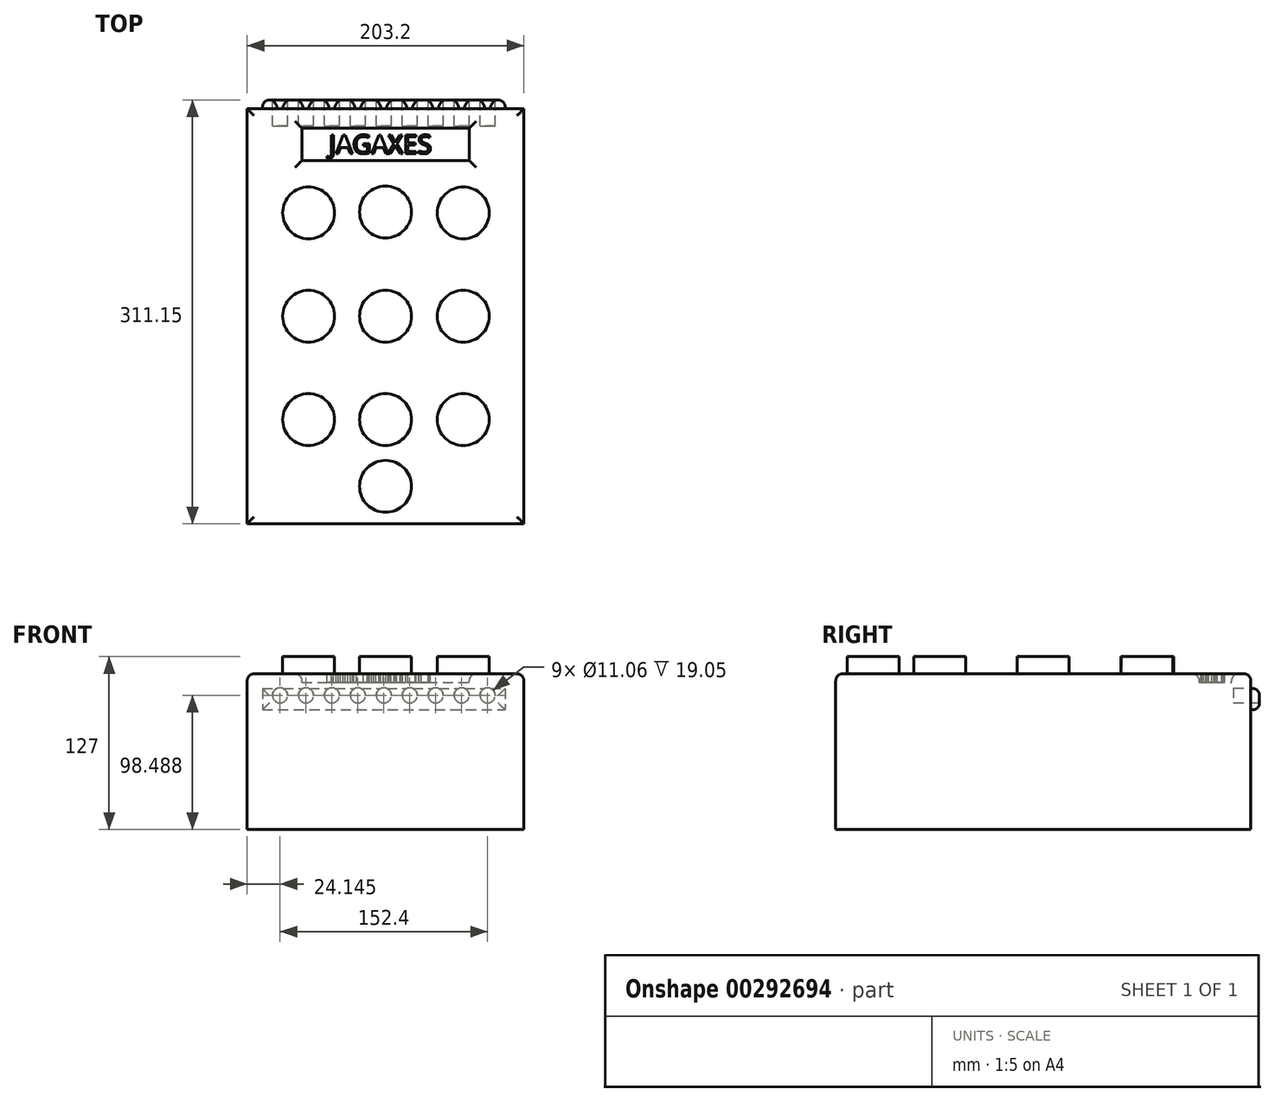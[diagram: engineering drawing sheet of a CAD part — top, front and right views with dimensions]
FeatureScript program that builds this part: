
annotation { "Feature Type Name" : "Feature", "Feature Type Description" : "" }
export const myFeature = defineFeature(function(context is Context, id is Id, definition is map)
    precondition{}
    {
        {
            var Q0;
            Q0=qCreatedBy(makeId("Top.planeOp"),FACE);
            var sketch = newSketch(context, id + "F0", { "sketchPlane" : qUnion([Q0])});
            skLineSegment(sketch, "E0.bottom", {"start": v(-101.6, 152.4) * mm, "end": v(101.6, 152.4) * mm});
            skLineSegment(sketch, "E0.top", {"start": v(-101.6, -152.4) * mm, "end": v(101.6, -152.4) * mm});
            skLineSegment(sketch, "E0.left", {"start": v(-101.6, 152.4) * mm, "end": v(-101.6, -152.4) * mm});
            skLineSegment(sketch, "E0.right", {"start": v(101.6, 152.4) * mm, "end": v(101.6, -152.4) * mm});
            skPoint(sketch, "E0.middle", {"position": v(0, 0) * mm});
            skSolve(sketch);
        }
        {
            var Q0;
            Q0=makeQuery(id+"F0.imprint","IMPRINT",FACE,{"disambiguationData":[TD([[makeQuery(id+"F0.imprint","IMPRINT",EDGE,{"derivedFrom":sQuery(id+"F0.wireOp",EDGE,"E0.bottom")}),-1.0]])]});
            extrude(context, id + "F1", {"entities" : qUnion([Q0]), "oppositeDirection" : true, "depth" : 114.3 * mm});
        }
        {
            var Q0;
            Q0=qCreatedBy(makeId("Top.planeOp"),FACE);
            var sketch = newSketch(context, id + "F2", { "sketchPlane" : qUnion([Q0])});
            skCircle(sketch, "E1", {"center": v(-56.48, 75.93) * mm, "radius": 19.05 * mm});
            skCircle(sketch, "E2", {"center": v(0, 76.56) * mm, "radius": 19.05 * mm});
            skCircle(sketch, "E3", {"center": v(57.1, 75.93) * mm, "radius": 19.05 * mm});
            skSolve(sketch);
        }
        {
            var Q0;
            Q0=makeQuery(id+"F2.imprint","IMPRINT",FACE,{"disambiguationData":[TD([[makeQuery(id+"F2.imprint","IMPRINT",EDGE,{"derivedFrom":sQuery(id+"F2.wireOp",EDGE,"E1")}),1.0]])]});
            extrude(context, id + "F3", {"entities" : qUnion([Q0]), "operationType" : NewBodyOperationType.ADD, "depth" : 12.7 * mm});
        }
        {
            var Q0;
            Q0 = qSketchRegion(id + "F2", true);
            extrude(context, id + "F4", {"entities" : qUnion([Q0]), "operationType" : NewBodyOperationType.ADD, "depth" : 12.7 * mm});
        }
        {
            var Q0;
            Q0=makeQuery(id+"F1.opExtrude","CAP_FACE",FACE,{"disambiguationData":[OSD([sQuery(id+"F0.wireOp",EDGE,"E0.bottom"),sQuery(id+"F0.wireOp",EDGE,"E0.top"),sQuery(id+"F0.wireOp",EDGE,"E0.left"),sQuery(id+"F0.wireOp",EDGE,"E0.right")])],"isStart":true});
            var sketch = newSketch(context, id + "F5", { "sketchPlane" : qUnion([Q0])});
            skCircle(sketch, "E4", {"center": v(0, 0) * mm, "radius": 19.05 * mm});
            skCircle(sketch, "E5", {"center": v(57.1, 0) * mm, "radius": 19.05 * mm});
            skCircle(sketch, "E6", {"center": v(-56.48, 0) * mm, "radius": 19.05 * mm});
            skCircle(sketch, "E7", {"center": v(-56.48, -75.93) * mm, "radius": 19.05 * mm});
            skCircle(sketch, "E8", {"center": v(0, -75.93) * mm, "radius": 19.05 * mm});
            skCircle(sketch, "E9", {"center": v(57.1, -75.93) * mm, "radius": 19.05 * mm});
            skSolve(sketch);
        }
        {
            var Q0;
            Q0=sQuery(id+"F5.wireOp",EDGE,"E6");
            var Q1;
            Q1=sQuery(id+"F5.wireOp",EDGE,"E7");
            extrude(context, id + "F6", {"bodyType" : ToolBodyType.SURFACE, "surfaceEntities" : qUnion([Q0, Q1]), "depth" : 12.7 * mm});
        }
        {
            var Q0;
            Q0 = qSketchRegion(id + "F5", true);
            extrude(context, id + "F7", {"entities" : qUnion([Q0]), "operationType" : NewBodyOperationType.ADD, "depth" : 12.7 * mm});
        }
        {
            var Q0;
            Q0=makeQuery(id+"F1.opExtrude","CAP_FACE",FACE,{"disambiguationData":[OSD([sQuery(id+"F0.wireOp",EDGE,"E0.bottom"),sQuery(id+"F0.wireOp",EDGE,"E0.top"),sQuery(id+"F0.wireOp",EDGE,"E0.left"),sQuery(id+"F0.wireOp",EDGE,"E0.right")])],"isStart":true});
            var sketch = newSketch(context, id + "F8", { "sketchPlane" : qUnion([Q0])});
            skCircle(sketch, "E10", {"center": v(0, -124.88) * mm, "radius": 19.05 * mm});
            skSolve(sketch);
        }
        {
            var Q0;
            Q0 = qSketchRegion(id + "F8", true);
            extrude(context, id + "F9", {"entities" : qUnion([Q0]), "operationType" : NewBodyOperationType.ADD, "depth" : 12.7 * mm});
        }
        {
            var Q0;
            Q0=makeQuery(id+"F1.opExtrude","CAP_EDGE",EDGE,{"disambiguationData":[OSD([sQuery(id+"F0.wireOp",EDGE,"E0.left")])],"isStart":true});
            var Q1;
            Q1=makeQuery(id+"F1.opExtrude","CAP_EDGE",EDGE,{"disambiguationData":[OSD([sQuery(id+"F0.wireOp",EDGE,"E0.top")])],"isStart":true});
            var Q2;
            Q2=makeQuery(id+"F1.opExtrude","CAP_EDGE",EDGE,{"disambiguationData":[OSD([sQuery(id+"F0.wireOp",EDGE,"E0.right")])],"isStart":true});
            var Q3;
            Q3=makeQuery(id+"F1.opExtrude","CAP_EDGE",EDGE,{"disambiguationData":[OSD([sQuery(id+"F0.wireOp",EDGE,"E0.bottom")])],"isStart":true});
            fillet(context, id + "F10", {"entities" : qUnion([Q0, Q1, Q2, Q3]), "radius" : 5.08 * mm, "tangentPropagation" : true, "allowEdgeOverflow" : false});
        }
        {
            var Q0;
            Q0=makeQuery(id+"F1.opExtrude","SWEPT_FACE",FACE,{"disambiguationData":[OSD([sQuery(id+"F0.wireOp",EDGE,"E0.bottom")])]});
            var sketch = newSketch(context, id + "F11", { "sketchPlane" : qUnion([Q0])});
            skLineSegment(sketch, "E11.bottom", {"start": v(90.36, -10.73) * mm, "end": v(-87.85, -10.73) * mm});
            skLineSegment(sketch, "E11.top", {"start": v(90.36, -26.42) * mm, "end": v(-87.85, -26.42) * mm});
            skLineSegment(sketch, "E11.left", {"start": v(90.36, -10.73) * mm, "end": v(90.36, -26.42) * mm});
            skLineSegment(sketch, "E11.right", {"start": v(-87.85, -10.73) * mm, "end": v(-87.85, -26.42) * mm});
            skSolve(sketch);
        }
        {
            var Q0;
            Q0 = qSketchRegion(id + "F11", true);
            extrude(context, id + "F12", {"entities" : qUnion([Q0]), "operationType" : NewBodyOperationType.ADD, "depth" : 6.35 * mm});
        }
        {
            var Q0;
            Q0=makeQuery(id+"F12.opExtrude","CAP_EDGE",EDGE,{"disambiguationData":[OSD([sQuery(id+"F11.wireOp",EDGE,"E11.bottom")])],"isStart":false});
            var Q1;
            Q1=makeQuery(id+"F12.opExtrude","CAP_EDGE",EDGE,{"disambiguationData":[OSD([sQuery(id+"F11.wireOp",EDGE,"E11.left")])],"isStart":false});
            var Q2;
            Q2=makeQuery(id+"F12.opExtrude","CAP_EDGE",EDGE,{"disambiguationData":[OSD([sQuery(id+"F11.wireOp",EDGE,"E11.top")])],"isStart":false});
            var Q3;
            Q3=makeQuery(id+"F12.opExtrude","CAP_EDGE",EDGE,{"disambiguationData":[OSD([sQuery(id+"F11.wireOp",EDGE,"E11.right")])],"isStart":false});
            fillet(context, id + "F13", {"entities" : qUnion([Q0, Q1, Q2, Q3]), "radius" : 5.08 * mm, "tangentPropagation" : true, "allowEdgeOverflow" : false});
        }
        {
            var Q0;
            Q0=makeQuery(id+"F12.opExtrude","CAP_FACE",FACE,{"disambiguationData":[OSD([sQuery(id+"F11.wireOp",EDGE,"E11.bottom"),sQuery(id+"F11.wireOp",EDGE,"E11.top"),sQuery(id+"F11.wireOp",EDGE,"E11.left"),sQuery(id+"F11.wireOp",EDGE,"E11.right")])],"isStart":false});
            var sketch = newSketch(context, id + "F14", { "sketchPlane" : qUnion([Q0])});
            skCircle(sketch, "E12", {"center": v(-74.94, -15.81) * mm, "radius": 5.53 * mm});
            skCircle(sketch, "E13.1.0.0", {"center": v(-55.9, -15.81) * mm, "radius": 5.53 * mm});
            skCircle(sketch, "E13.2.0.0", {"center": v(-36.84, -15.81) * mm, "radius": 5.53 * mm});
            skLineSegment(sketch, "E13.direction1", {"start": v(-74.94, -15.81) * mm, "end": v(-55.9, -15.81) * mm, "construction": true});
            skCircle(sketch, "E14.0.3.0", {"center": v(-17.8, -15.81) * mm, "radius": 5.53 * mm});
            skCircle(sketch, "E14.0.4.0", {"center": v(1.26, -15.81) * mm, "radius": 5.53 * mm});
            skCircle(sketch, "E14.0.5.0", {"center": v(20.3, -15.81) * mm, "radius": 5.53 * mm});
            skCircle(sketch, "E14.0.6.0", {"center": v(39.36, -15.81) * mm, "radius": 5.53 * mm});
            skCircle(sketch, "E14.0.7.0", {"center": v(58.4, -15.81) * mm, "radius": 5.53 * mm});
            skCircle(sketch, "E14.0.8.0", {"center": v(77.46, -15.81) * mm, "radius": 5.53 * mm});
            skSolve(sketch);
        }
        {
            var Q0;
            Q0 = qSketchRegion(id + "F14", true);
            extrude(context, id + "F15", {"entities" : qUnion([Q0]), "operationType" : NewBodyOperationType.REMOVE, "oppositeDirection" : true, "depth" : 19.05 * mm});
        }
        {
            var Q0;
            Q0=makeQuery(id+"F1.opExtrude","CAP_FACE",FACE,{"disambiguationData":[OSD([sQuery(id+"F0.wireOp",EDGE,"E0.bottom"),sQuery(id+"F0.wireOp",EDGE,"E0.top"),sQuery(id+"F0.wireOp",EDGE,"E0.left"),sQuery(id+"F0.wireOp",EDGE,"E0.right")])],"isStart":true});
            var sketch = newSketch(context, id + "F16", { "sketchPlane" : qUnion([Q0])});
            skLineSegment(sketch, "E15.bottom", {"start": v(-61.5, 114.33) * mm, "end": v(61.5, 114.33) * mm});
            skLineSegment(sketch, "E15.top", {"start": v(-61.5, 138.18) * mm, "end": v(61.5, 138.18) * mm});
            skLineSegment(sketch, "E15.left", {"start": v(-61.5, 114.33) * mm, "end": v(-61.5, 138.18) * mm});
            skLineSegment(sketch, "E15.right", {"start": v(61.5, 114.33) * mm, "end": v(61.5, 138.18) * mm});
            skPoint(sketch, "E15.middle", {"position": v(0, 126.26) * mm});
            skText(sketch, "E16", { "text": "   JAGAXES", "fontName": "OpenSans-Regular.ttf"});
            const initialGuessF16  = {"E16": [-0.05648, 0.11945, 1, 0, 0.0138]};
            skSetInitialGuess(sketch, initialGuessF16);
            skSolve(sketch);
        }
        {
            var Q0;
            Q0 = qSketchRegion(id + "F16", true);
            extrude(context, id + "F17", {"entities" : qUnion([Q0]), "operationType" : NewBodyOperationType.REMOVE, "oppositeDirection" : true, "depth" : 6.35 * mm});
        }
        {
            var Q0;
            Q0=makeQuery(id+"F17.boolean.opBoolean","COPY",EDGE,{"derivedFrom":makeQuery(id+"F17.opExtrude","CAP_EDGE",EDGE,{"disambiguationData":[OSD([sQuery(id+"F16.wireOp",EDGE,"E15.top")])],"isStart":true})});
            var Q1;
            Q1=makeQuery(id+"F17.boolean.opBoolean","COPY",EDGE,{"derivedFrom":makeQuery(id+"F17.opExtrude","CAP_EDGE",EDGE,{"disambiguationData":[OSD([sQuery(id+"F16.wireOp",EDGE,"E15.left")])],"isStart":true})});
            var Q2;
            Q2=makeQuery(id+"F17.boolean.opBoolean","COPY",EDGE,{"derivedFrom":makeQuery(id+"F17.opExtrude","CAP_EDGE",EDGE,{"disambiguationData":[OSD([sQuery(id+"F16.wireOp",EDGE,"E15.bottom")])],"isStart":true})});
            var Q3;
            Q3=makeQuery(id+"F17.boolean.opBoolean","COPY",EDGE,{"derivedFrom":makeQuery(id+"F17.opExtrude","CAP_EDGE",EDGE,{"disambiguationData":[OSD([sQuery(id+"F16.wireOp",EDGE,"E15.right")])],"isStart":true})});
            fillet(context, id + "F18", {"entities" : qUnion([Q0, Q1, Q2, Q3]), "radius" : 5.08 * mm, "tangentPropagation" : true, "allowEdgeOverflow" : false});
        }
    });
